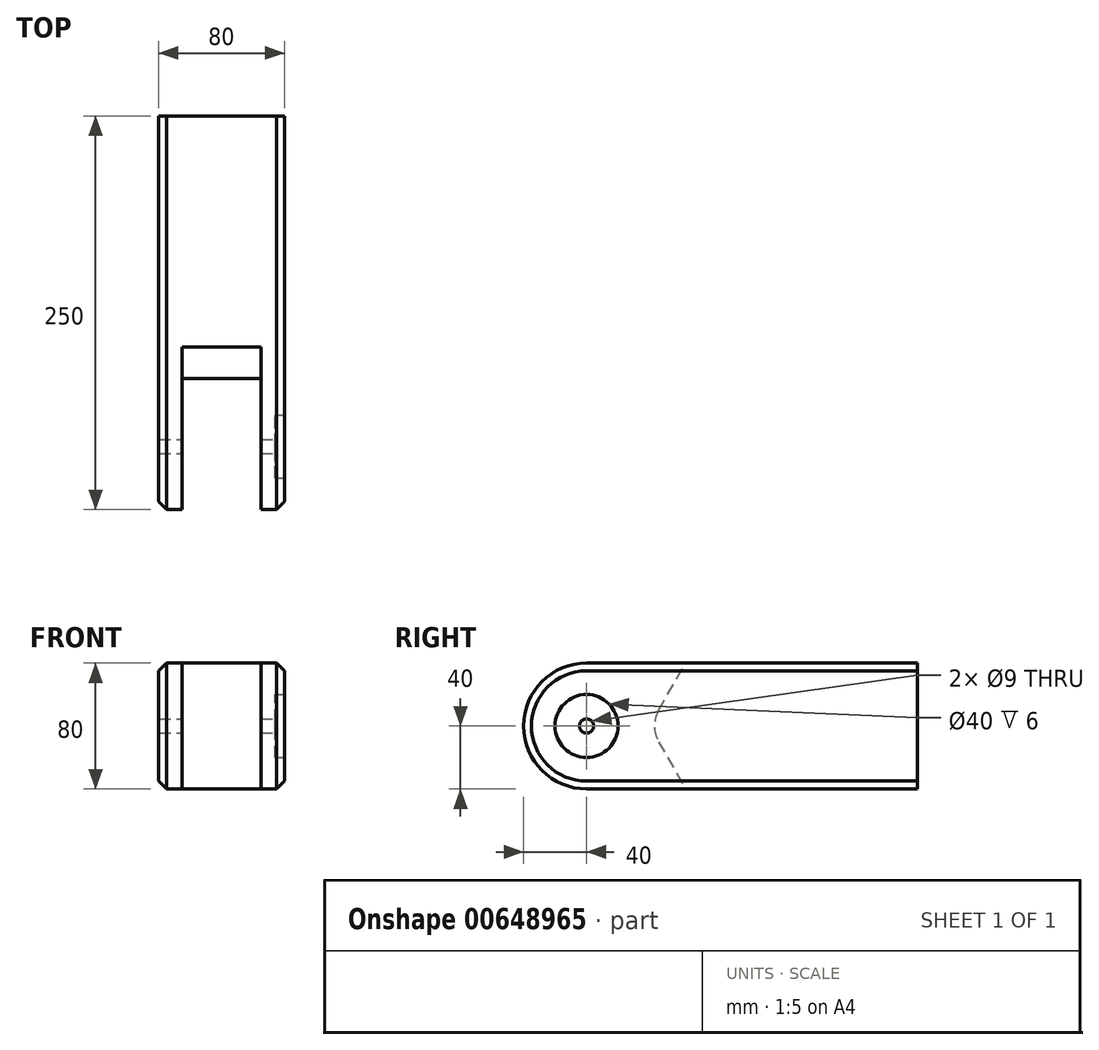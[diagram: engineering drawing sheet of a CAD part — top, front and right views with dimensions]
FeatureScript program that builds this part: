
annotation { "Feature Type Name" : "Feature", "Feature Type Description" : "" }
export const myFeature = defineFeature(function(context is Context, id is Id, definition is map)
    precondition{}
    {
        {
            var Q0;
            Q0=qCreatedBy(makeId("Right.planeOp"),FACE);
            var sketch = newSketch(context, id + "F0", { "sketchPlane" : qUnion([Q0])});
            skLineSegment(sketch, "E0.bottom", {"start": v(-125, 40) * mm, "end": v(125, 40) * mm});
            skLineSegment(sketch, "E0.top", {"start": v(-125, -40) * mm, "end": v(125, -40) * mm});
            skLineSegment(sketch, "E0.left", {"start": v(-125, 40) * mm, "end": v(-125, -40) * mm});
            skLineSegment(sketch, "E0.right", {"start": v(125, 40) * mm, "end": v(125, -40) * mm});
            skPoint(sketch, "E0.middle", {"position": v(0, 0) * mm});
            skSolve(sketch);
        }
        {
            var Q0;
            Q0 = qSketchRegion(id + "F0", true);
            extrude(context, id + "F1", {"entities" : qUnion([Q0]), "endBound" : BoundingType.SYMMETRIC, "depth" : 80 * mm, "offsetDistance" : 25 * mm});
        }
        {
            var Q0;
            Q0=makeQuery(id+"F1.opExtrude","SWEPT_EDGE",EDGE,{"disambiguationData":[OSD([sQuery(id+"F0.wireOp",EDGE,"E0.bottom"),sQuery(id+"F0.wireOp",EDGE,"E0.left")])]});
            var Q1;
            Q1=makeQuery(id+"F1.opExtrude","SWEPT_EDGE",EDGE,{"disambiguationData":[OSD([sQuery(id+"F0.wireOp",EDGE,"E0.top"),sQuery(id+"F0.wireOp",EDGE,"E0.left")])]});
            fillet(context, id + "F2", {"entities" : qUnion([Q0, Q1]), "radius" : 40 * mm, "tangentPropagation" : true, "allowEdgeOverflow" : false});
        }
        {
            var Q0;
            Q0=qCreatedBy(makeId("Right.planeOp"),FACE);
            var sketch = newSketch(context, id + "F3", { "sketchPlane" : qUnion([Q0])});
            skLineSegment(sketch, "E1", {"start": v(0, 0) * mm, "end": v(-85, 0) * mm, "construction": true});
            skLineSegment(sketch, "E2", {"start": v(-85, 0) * mm, "end": v(-61.9, 40) * mm, "construction": true});
            skLineSegment(sketch, "E3", {"start": v(-45, 0) * mm, "end": v(-21.9, 40) * mm});
            skLineSegment(sketch, "E4.MirrorCS", {"start": v(-45, 0) * mm, "end": v(-21.9, -40) * mm});
            skLineSegment(sketch, "E5", {"start": v(-21.9, 40) * mm, "end": v(-155.97, 40) * mm});
            skLineSegment(sketch, "E6", {"start": v(-155.97, 40) * mm, "end": v(-155.97, -40) * mm});
            skLineSegment(sketch, "E7", {"start": v(-155.97, -40) * mm, "end": v(-21.9, -40) * mm});
            skSolve(sketch);
        }
        {
            var Q0;
            Q0 = qSketchRegion(id + "F3", true);
            extrude(context, id + "F4", {"entities" : qUnion([Q0]), "operationType" : NewBodyOperationType.REMOVE, "endBound" : BoundingType.SYMMETRIC, "oppositeDirection" : true, "depth" : 50 * mm, "offsetDistance" : 25 * mm});
        }
        {
            var Q0;
            Q0=makeQuery(id+"F4.boolean.opBoolean","COPY",EDGE,{"derivedFrom":makeQuery(id+"F4.opExtrude","SWEPT_EDGE",EDGE,{"disambiguationData":[OSD([sQuery(id+"F3.wireOp",EDGE,"E3"),sQuery(id+"F3.wireOp",EDGE,"E4.MirrorCS")])]})});
            fillet(context, id + "F5", {"entities" : qUnion([Q0]), "radius" : 20 * mm, "tangentPropagation" : true, "allowEdgeOverflow" : false});
        }
        {
            var Q0;
            Q0=makeQuery(id+"F1.opExtrude","CAP_EDGE",EDGE,{"disambiguationData":[OSD([sQuery(id+"F0.wireOp",EDGE,"E0.bottom")])],"isStart":false});
            var Q1;
            Q1=makeQuery(id+"F1.opExtrude","CAP_EDGE",EDGE,{"disambiguationData":[OSD([sQuery(id+"F0.wireOp",EDGE,"E0.bottom")])],"isStart":true});
            chamfer(context, id + "F6", {"entities" : qUnion([Q0, Q1]), "width" : 5 * mm, "tangentPropagation" : true});
        }
        {
            var Q0;
            Q0=makeQuery(id+"F1.opExtrude","CAP_FACE",FACE,{"disambiguationData":[OSD([sQuery(id+"F0.wireOp",EDGE,"E0.bottom"),sQuery(id+"F0.wireOp",EDGE,"E0.top"),sQuery(id+"F0.wireOp",EDGE,"E0.left"),sQuery(id+"F0.wireOp",EDGE,"E0.right")])],"isStart":false});
            var sketch = newSketch(context, id + "F7", { "sketchPlane" : qUnion([Q0])});
            skCircle(sketch, "E8", {"center": v(-85, 0) * mm, "radius": 4.5 * mm});
            skSolve(sketch);
        }
        {
            var Q0;
            Q0 = qSketchRegion(id + "F7", true);
            extrude(context, id + "F8", {"entities" : qUnion([Q0]), "operationType" : NewBodyOperationType.REMOVE, "endBound" : BoundingType.THROUGH_ALL, "oppositeDirection" : true, "depth" : 25 * mm, "offsetDistance" : 25 * mm});
        }
        {
            var Q0;
            Q0=makeQuery(id+"F1.opExtrude","CAP_FACE",FACE,{"disambiguationData":[OSD([sQuery(id+"F0.wireOp",EDGE,"E0.bottom"),sQuery(id+"F0.wireOp",EDGE,"E0.top"),sQuery(id+"F0.wireOp",EDGE,"E0.left"),sQuery(id+"F0.wireOp",EDGE,"E0.right")])],"isStart":false});
            var sketch = newSketch(context, id + "F9", { "sketchPlane" : qUnion([Q0])});
            skCircle(sketch, "E9", {"center": v(-85, 0) * mm, "radius": 20 * mm});
            skSolve(sketch);
        }
        {
            var Q0;
            Q0 = qSketchRegion(id + "F9", true);
            extrude(context, id + "F10", {"entities" : qUnion([Q0]), "operationType" : NewBodyOperationType.REMOVE, "oppositeDirection" : true, "depth" : 6 * mm, "offsetDistance" : 25 * mm});
        }
    });
